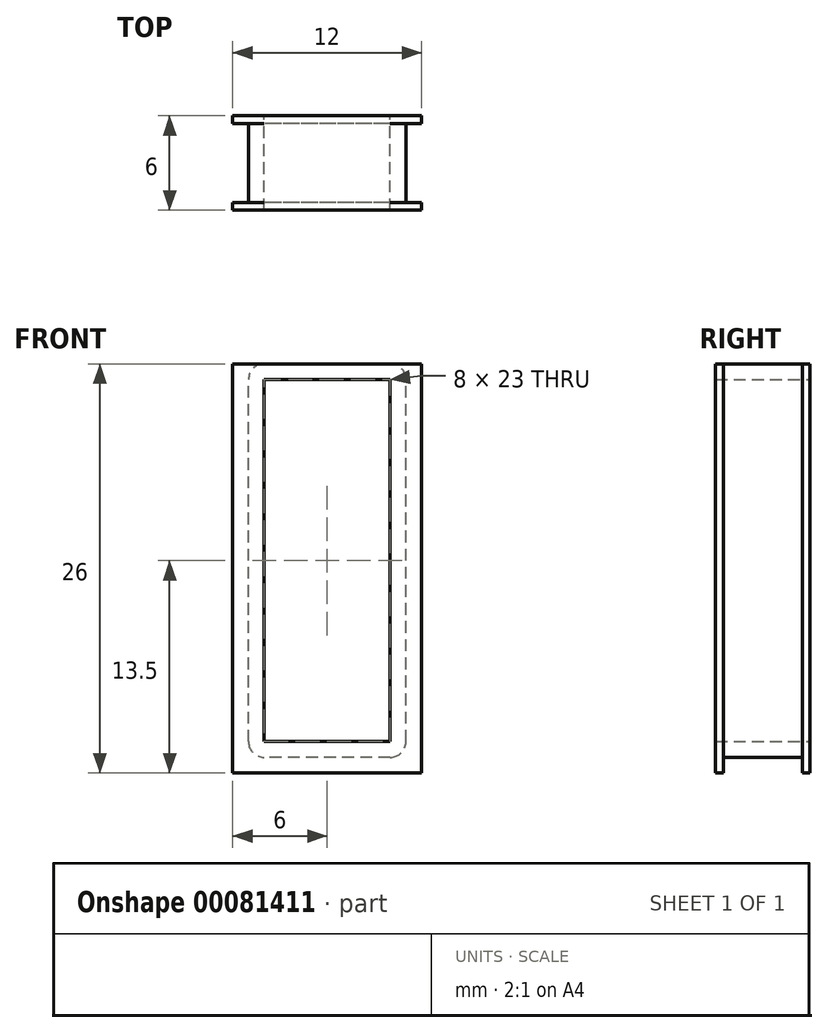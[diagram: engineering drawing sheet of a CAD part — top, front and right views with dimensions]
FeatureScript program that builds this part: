
annotation { "Feature Type Name" : "Feature", "Feature Type Description" : "" }
export const myFeature = defineFeature(function(context is Context, id is Id, definition is map)
    precondition{}
    {
        {
            var Q0;
            Q0=qCreatedBy(makeId("Front.planeOp"),FACE);
            var sketch = newSketch(context, id + "F0", { "sketchPlane" : qUnion([Q0])});
            skLineSegment(sketch, "E0.bottom", {"start": v(5, -12.5) * mm, "end": v(-5, -12.5) * mm});
            skLineSegment(sketch, "E0.top", {"start": v(5, 12.5) * mm, "end": v(-5, 12.5) * mm});
            skLineSegment(sketch, "E0.left", {"start": v(5, -12.5) * mm, "end": v(5, 12.5) * mm});
            skLineSegment(sketch, "E0.right", {"start": v(-5, -12.5) * mm, "end": v(-5, 12.5) * mm});
            skPoint(sketch, "E0.middle", {"position": v(0, 0) * mm});
            skLineSegment(sketch, "E1.0", {"start": v(-4, -11.5) * mm, "end": v(-4, 11.5) * mm});
            skLineSegment(sketch, "E1.1", {"start": v(4, -11.5) * mm, "end": v(-4, -11.5) * mm});
            skLineSegment(sketch, "E1.2", {"start": v(4, -11.5) * mm, "end": v(4, 11.5) * mm});
            skLineSegment(sketch, "E1.3", {"start": v(4, 11.5) * mm, "end": v(-4, 11.5) * mm});
            skSolve(sketch);
        }
        {
            var Q0;
            Q0=makeQuery(id+"F0.imprint","IMPRINT",FACE,{"disambiguationData":[TD([[makeQuery(id+"F0.imprint","IMPRINT",EDGE,{"derivedFrom":sQuery(id+"F0.wireOp",EDGE,"E0.bottom")}),-1.0]])]});
            extrude(context, id + "F1", {"entities" : qUnion([Q0]), "depth" : 5 * mm});
        }
        {
            var Q0;
            Q0=makeQuery(id+"F1.opExtrude","CAP_FACE",FACE,{"disambiguationData":[OSD([sQuery(id+"F0.wireOp",EDGE,"E0.bottom"),sQuery(id+"F0.wireOp",EDGE,"E0.top"),sQuery(id+"F0.wireOp",EDGE,"E0.left"),sQuery(id+"F0.wireOp",EDGE,"E0.right"),sQuery(id+"F0.wireOp",EDGE,"E1.0"),sQuery(id+"F0.wireOp",EDGE,"E1.1"),sQuery(id+"F0.wireOp",EDGE,"E1.2"),sQuery(id+"F0.wireOp",EDGE,"E1.3")])],"isStart":true});
            var sketch = newSketch(context, id + "F2", { "sketchPlane" : qUnion([Q0])});
            skLineSegment(sketch, "E2.0", {"start": v(5, -12.5) * mm, "end": v(5, 12.5) * mm});
            skLineSegment(sketch, "E3.0", {"start": v(-5, 12.5) * mm, "end": v(5, 12.5) * mm});
            skLineSegment(sketch, "E4.0", {"start": v(-5, -12.5) * mm, "end": v(-5, 12.5) * mm});
            skLineSegment(sketch, "E5.0", {"start": v(-5, -12.5) * mm, "end": v(5, -12.5) * mm});
            skLineSegment(sketch, "E6.0", {"start": v(-6, -13.5) * mm, "end": v(-6, 13.5) * mm});
            skLineSegment(sketch, "E6.1", {"start": v(-6, -13.5) * mm, "end": v(6, -13.5) * mm});
            skLineSegment(sketch, "E6.2", {"start": v(6, -13.5) * mm, "end": v(6, 13.5) * mm});
            skLineSegment(sketch, "E6.3", {"start": v(-6, 13.5) * mm, "end": v(6, 13.5) * mm});
            skSolve(sketch);
        }
        {
            var Q0;
            Q0=makeQuery(id+"F2.imprint","IMPRINT",FACE,{"disambiguationData":[TD([[makeQuery(id+"F2.imprint","IMPRINT",EDGE,{"derivedFrom":sQuery(id+"F2.wireOp",EDGE,"E2.0")}),-1.0]])]});
            var Q1;
            Q1=makeQuery(id+"F2.imprint","IMPRINT",FACE,{"disambiguationData":[TD([[makeQuery(id+"F2.imprint","IMPRINT",EDGE,{"derivedFrom":sQuery(id+"F2.wireOp",EDGE,"E2.0")}),1.0]])]});
            extrude(context, id + "F3", {"entities" : qUnion([Q0, Q1]), "operationType" : NewBodyOperationType.ADD, "depth" : 0.5 * mm});
        }
        {
            var Q0;
            Q0=makeQuery(id+"F1.opExtrude","CAP_FACE",FACE,{"disambiguationData":[OSD([sQuery(id+"F0.wireOp",EDGE,"E0.bottom"),sQuery(id+"F0.wireOp",EDGE,"E0.top"),sQuery(id+"F0.wireOp",EDGE,"E0.left"),sQuery(id+"F0.wireOp",EDGE,"E0.right"),sQuery(id+"F0.wireOp",EDGE,"E1.0"),sQuery(id+"F0.wireOp",EDGE,"E1.1"),sQuery(id+"F0.wireOp",EDGE,"E1.2"),sQuery(id+"F0.wireOp",EDGE,"E1.3")])],"isStart":false});
            var sketch = newSketch(context, id + "F4", { "sketchPlane" : qUnion([Q0])});
            skLineSegment(sketch, "E7.0", {"start": v(-6, -13.5) * mm, "end": v(-6, 13.5) * mm});
            skLineSegment(sketch, "E8.0", {"start": v(6, -13.5) * mm, "end": v(-6, -13.5) * mm});
            skLineSegment(sketch, "E9.0", {"start": v(6, -13.5) * mm, "end": v(6, 13.5) * mm});
            skLineSegment(sketch, "E10.0", {"start": v(6, 13.5) * mm, "end": v(-6, 13.5) * mm});
            skLineSegment(sketch, "E11.0", {"start": v(5, 12.5) * mm, "end": v(-5, 12.5) * mm});
            skLineSegment(sketch, "E12.0", {"start": v(-5, -12.5) * mm, "end": v(-5, 12.5) * mm});
            skLineSegment(sketch, "E13.0", {"start": v(5, -12.5) * mm, "end": v(-5, -12.5) * mm});
            skLineSegment(sketch, "E14.0", {"start": v(5, -12.5) * mm, "end": v(5, 12.5) * mm});
            skSolve(sketch);
        }
        {
            var Q0;
            Q0=makeQuery(id+"F4.imprint","IMPRINT",FACE,{"disambiguationData":[TD([[makeQuery(id+"F4.imprint","IMPRINT",EDGE,{"derivedFrom":sQuery(id+"F4.wireOp",EDGE,"E7.0")}),-1.0]])]});
            var Q1;
            Q1=makeQuery(id+"F4.imprint","IMPRINT",FACE,{"disambiguationData":[TD([[makeQuery(id+"F4.imprint","IMPRINT",EDGE,{"derivedFrom":sQuery(id+"F4.wireOp",EDGE,"E11.0")}),1.0]])]});
            extrude(context, id + "F5", {"entities" : qUnion([Q0, Q1]), "operationType" : NewBodyOperationType.ADD, "depth" : 0.5 * mm});
        }
        {
            var Q0;
            Q0=makeQuery(id+"F5.opExtrude","CAP_FACE",FACE,{"disambiguationData":[OSD([sQuery(id+"F0.wireOp",EDGE,"E1.0"),sQuery(id+"F0.wireOp",EDGE,"E1.1"),sQuery(id+"F0.wireOp",EDGE,"E1.2"),sQuery(id+"F0.wireOp",EDGE,"E1.3"),sQuery(id+"F4.wireOp",EDGE,"E7.0"),sQuery(id+"F4.wireOp",EDGE,"E8.0"),sQuery(id+"F4.wireOp",EDGE,"E9.0"),sQuery(id+"F4.wireOp",EDGE,"E10.0")])],"isStart":false});
            var sketch = newSketch(context, id + "F6", { "sketchPlane" : qUnion([Q0])});
            skLineSegment(sketch, "E15.bottom", {"start": v(-6, -0.5) * mm, "end": v(-5, -0.5) * mm});
            skLineSegment(sketch, "E15.top", {"start": v(-6, 0.5) * mm, "end": v(-5, 0.5) * mm});
            skLineSegment(sketch, "E15.left", {"start": v(-6, -0.5) * mm, "end": v(-6, 0.5) * mm});
            skLineSegment(sketch, "E15.right", {"start": v(-5, -0.5) * mm, "end": v(-5, 0.5) * mm});
            skLineSegment(sketch, "E16.MirrorCS", {"start": v(5, -0.5) * mm, "end": v(5, 0.5) * mm});
            skLineSegment(sketch, "E17.MirrorCS", {"start": v(6, -0.5) * mm, "end": v(6, 0.5) * mm});
            skLineSegment(sketch, "E18.MirrorCS", {"start": v(6, -0.5) * mm, "end": v(5, -0.5) * mm});
            skLineSegment(sketch, "E19.MirrorCS", {"start": v(6, 0.5) * mm, "end": v(5, 0.5) * mm});
            skLineSegment(sketch, "E20.bottom", {"start": v(-6, -2.5) * mm, "end": v(-5, -2.5) * mm});
            skLineSegment(sketch, "E20.top", {"start": v(-6, -1.5) * mm, "end": v(-5, -1.5) * mm});
            skLineSegment(sketch, "E20.left", {"start": v(-6, -2.5) * mm, "end": v(-6, -1.5) * mm});
            skLineSegment(sketch, "E20.right", {"start": v(-5, -2.5) * mm, "end": v(-5, -1.5) * mm});
            skLineSegment(sketch, "E21.MirrorCS", {"start": v(-6, 2.5) * mm, "end": v(-5, 2.5) * mm});
            skLineSegment(sketch, "E22.MirrorCS", {"start": v(-6, 1.5) * mm, "end": v(-5, 1.5) * mm});
            skLineSegment(sketch, "E23.MirrorCS", {"start": v(-5, 2.5) * mm, "end": v(-5, 1.5) * mm});
            skLineSegment(sketch, "E24.MirrorCS", {"start": v(-6, 2.5) * mm, "end": v(-6, 1.5) * mm});
            skLineSegment(sketch, "E25.MirrorCS", {"start": v(6, 2.5) * mm, "end": v(6, 1.5) * mm});
            skLineSegment(sketch, "E26.MirrorCS", {"start": v(6, 1.5) * mm, "end": v(5, 1.5) * mm});
            skLineSegment(sketch, "E27.MirrorCS", {"start": v(5, 2.5) * mm, "end": v(5, 1.5) * mm});
            skLineSegment(sketch, "E28.MirrorCS", {"start": v(6, 2.5) * mm, "end": v(5, 2.5) * mm});
            skLineSegment(sketch, "E29.MirrorCS", {"start": v(6, -2.5) * mm, "end": v(6, -1.5) * mm});
            skLineSegment(sketch, "E30.MirrorCS", {"start": v(6, -1.5) * mm, "end": v(5, -1.5) * mm});
            skLineSegment(sketch, "E31.MirrorCS", {"start": v(5, -2.5) * mm, "end": v(5, -1.5) * mm});
            skLineSegment(sketch, "E32.MirrorCS", {"start": v(6, -2.5) * mm, "end": v(5, -2.5) * mm});
            skSolve(sketch);
        }
        {
            var Q0;
            Q0=makeQuery(id+"F3.opExtrude","CAP_FACE",FACE,{"disambiguationData":[OSD([sQuery(id+"F0.wireOp",EDGE,"E1.0"),sQuery(id+"F0.wireOp",EDGE,"E1.1"),sQuery(id+"F0.wireOp",EDGE,"E1.2"),sQuery(id+"F0.wireOp",EDGE,"E1.3"),sQuery(id+"F2.wireOp",EDGE,"E6.0"),sQuery(id+"F2.wireOp",EDGE,"E6.1"),sQuery(id+"F2.wireOp",EDGE,"E6.2"),sQuery(id+"F2.wireOp",EDGE,"E6.3")])],"isStart":false});
            var sketch = newSketch(context, id + "F7", { "sketchPlane" : qUnion([Q0])});
            skLineSegment(sketch, "E33.bottom", {"start": v(6, 13.5) * mm, "end": v(-6, 13.5) * mm});
            skLineSegment(sketch, "E33.top", {"start": v(6, 12.5) * mm, "end": v(-6, 12.5) * mm});
            skLineSegment(sketch, "E33.left", {"start": v(6, 13.5) * mm, "end": v(6, 12.5) * mm});
            skLineSegment(sketch, "E33.right", {"start": v(-6, 13.5) * mm, "end": v(-6, 12.5) * mm});
            skSolve(sketch);
        }
        {
            var Q0;
            Q0 = qSketchRegion(id + "F7", true);
            extrude(context, id + "F8", {"entities" : qUnion([Q0]), "operationType" : NewBodyOperationType.REMOVE, "oppositeDirection" : true, "depth" : 25 * mm});
        }
        {
            var Q0;
            Q0=makeQuery(id+"F1.opExtrude","SWEPT_EDGE",EDGE,{"disambiguationData":[OSD([sQuery(id+"F0.wireOp",EDGE,"E0.top"),sQuery(id+"F0.wireOp",EDGE,"E0.right")])]});
            var Q1;
            Q1=makeQuery(id+"F1.opExtrude","SWEPT_EDGE",EDGE,{"disambiguationData":[OSD([sQuery(id+"F0.wireOp",EDGE,"E0.top"),sQuery(id+"F0.wireOp",EDGE,"E0.left")])]});
            var Q2;
            Q2=makeQuery(id+"F1.opExtrude","SWEPT_EDGE",EDGE,{"disambiguationData":[OSD([sQuery(id+"F0.wireOp",EDGE,"E0.bottom"),sQuery(id+"F0.wireOp",EDGE,"E0.right")])]});
            var Q3;
            Q3=makeQuery(id+"F1.opExtrude","SWEPT_EDGE",EDGE,{"disambiguationData":[OSD([sQuery(id+"F0.wireOp",EDGE,"E0.bottom"),sQuery(id+"F0.wireOp",EDGE,"E0.left")])]});
            fillet(context, id + "F9", {"entities" : qUnion([Q0, Q1, Q2, Q3]), "radius" : 1 * mm, "tangentPropagation" : true, "allowEdgeOverflow" : false});
        }
    });
